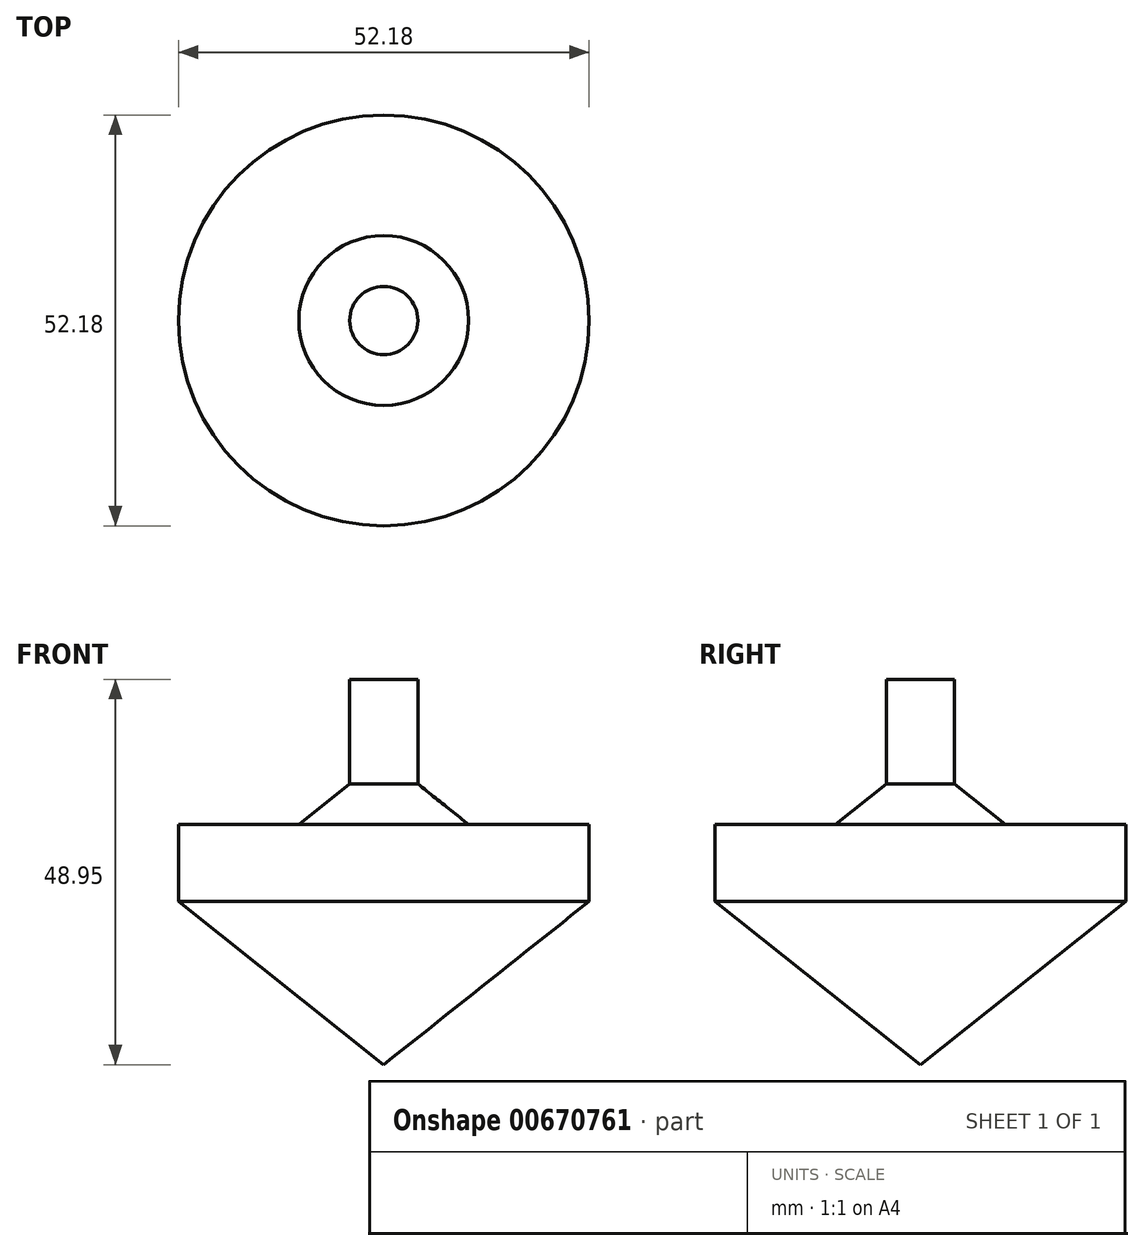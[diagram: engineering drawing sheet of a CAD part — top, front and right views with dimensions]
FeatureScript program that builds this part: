
annotation { "Feature Type Name" : "Feature", "Feature Type Description" : "" }
export const myFeature = defineFeature(function(context is Context, id is Id, definition is map)
    precondition{}
    {
        {
            var Q0;
            Q0=qCreatedBy(makeId("Front.planeOp"),FACE);
            var sketch = newSketch(context, id + "F0", { "sketchPlane" : qUnion([Q0])});
            skLineSegment(sketch, "E0", {"start": v(0, 0) * mm, "end": v(31.75, 0) * mm});
            skLineSegment(sketch, "E1", {"start": v(0, 0) * mm, "end": v(-31.75, 0) * mm});
            skLineSegment(sketch, "E2", {"start": v(-31.75, 0) * mm, "end": v(-31.75, 63.5) * mm});
            skLineSegment(sketch, "E3", {"start": v(31.75, 0) * mm, "end": v(31.75, 63.5) * mm});
            skLineSegment(sketch, "E4", {"start": v(0, 0) * mm, "end": v(26.09, 20.74) * mm});
            skLineSegment(sketch, "E5", {"start": v(26.09, 20.74) * mm, "end": v(26.09, 30.51) * mm});
            skLineSegment(sketch, "E6", {"start": v(26.09, 30.51) * mm, "end": v(10.78, 30.51) * mm});
            skLineSegment(sketch, "E7", {"start": v(10.78, 30.51) * mm, "end": v(4.33, 35.67) * mm});
            skLineSegment(sketch, "E8", {"start": v(4.33, 35.67) * mm, "end": v(4.33, 48.95) * mm});
            skLineSegment(sketch, "E9", {"start": v(4.33, 48.95) * mm, "end": v(0, 48.95) * mm});
            skLineSegment(sketch, "E10", {"start": v(0, 48.95) * mm, "end": v(0, 0) * mm});
            skSolve(sketch);
        }
        {
            var Q0;
            Q0=qSketchRegion(id+"F0",true);
            var Q1;
            Q1=sQuery(id+"F0.wireOp",EDGE,"E10");
            revolve(context, id + "F1", {"entities" : qUnion([Q0]), "axis" : qUnion([Q1]), "revolveType" : RevolveType.FULL});
        }
    });
